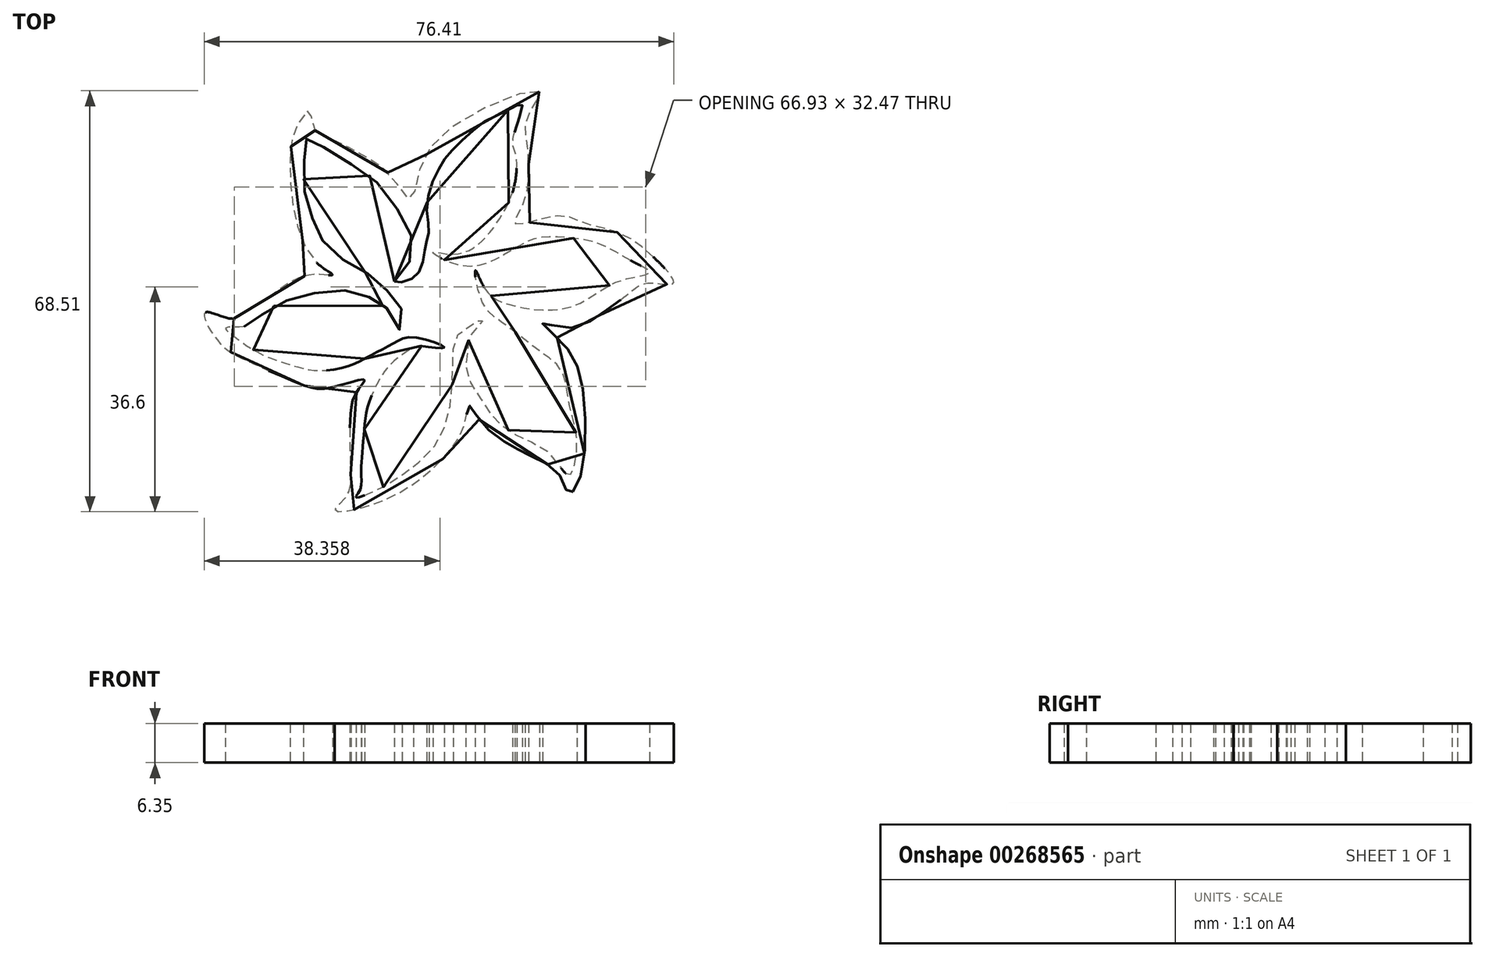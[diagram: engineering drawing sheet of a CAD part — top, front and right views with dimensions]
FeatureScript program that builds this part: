
annotation { "Feature Type Name" : "Feature", "Feature Type Description" : "" }
export const myFeature = defineFeature(function(context is Context, id is Id, definition is map)
    precondition{}
    {
        {
            var Q0;
            Q0=qCreatedBy(makeId("Top.planeOp"),FACE);
            var sketch = newSketch(context, id + "F0", { "sketchPlane" : qUnion([Q0])});
            skPoint(sketch, "E0.34.internal.snap0", {"position": v(38.1, 68.07) * mm});
            skFitSpline(sketch, "E0", {"points": [v(54.35, 68.07) * mm, v(40.9, 62.9) * mm, v(34.76, 54.83) * mm, v(33.41, 50.6) * mm, v(30.53, 54.06) * mm, v(26.11, 57.52) * mm, v(20.54, 60.4) * mm, v(17.47, 62.51) * mm, v(17.09, 65.2) * mm, v(15.36, 63.28) * mm, v(14.01, 59.44) * mm, v(14.01, 51.95) * mm, v(15.36, 45.23) * mm, v(18.43, 40.04) * mm, v(20.74, 38.32) * mm, v(17.09, 38.32) * mm, v(11.13, 35.24) * mm, v(6.52, 32.17) * mm, v(4.03, 31.2) * mm, v(0, 32.17) * mm, v(2.1, 27.56) * mm, v(6.14, 24.68) * mm, v(11.13, 22.37) * mm, v(15.74, 20.45) * mm, v(19.97, 19.88) * mm, v(25.92, 21.22) * mm, v(24.58, 19.1) * mm, v(23.62, 14.3) * mm, v(23.62, 8.35) * mm, v(23.62, 3.94) * mm, v(22.47, 1.63) * mm, v(21.12, 0) * mm, v(23.76, 0) * mm, v(31.1, 2.6) * mm, v(38.1, 7.77) * mm, v(42.19, 13.88) * mm, v(43.02, 17) * mm, v(44.75, 14.54) * mm, v(49.54, 10.66) * mm, v(53, 8.86) * mm, v(57.66, 5.75) * mm, v(59.15, 2.79) * mm, v(60.88, 4.9) * mm, v(61.45, 19.69) * mm, v(58.19, 27.18) * mm, v(54.92, 30.44) * mm, v(58.96, 29.67) * mm, v(65.3, 32.55) * mm, v(69.13, 35.43) * mm, v(72.02, 36.97) * mm, v(76.2, 36.97) * mm, v(73.36, 40.81) * mm, v(67.6, 45.04) * mm, v(61.64, 46.77) * mm, v(57.23, 47.92) * mm, v(50.5, 46.57) * mm, v(51.85, 50.03) * mm, v(52.62, 55.4) * mm, v(52.43, 59.63) * mm, v(52.43, 63.86) * mm, v(54.35, 68.07) * mm]});
            skFitSpline(sketch, "E1", {"points": [v(30.83, 37.2) * mm, v(33.13, 40.17) * mm, v(33.63, 44.46) * mm, v(31, 49.4) * mm, v(26.7, 54.5) * mm, v(21.44, 57.63) * mm, v(17.32, 60.4) * mm, v(16.5, 60.4) * mm, v(16.17, 57.8) * mm, v(16.17, 51.95) * mm, v(17.48, 47.42) * mm, v(18.97, 44.13) * mm, v(22.42, 40.83) * mm, v(26.7, 38.36) * mm, v(29.67, 35.73) * mm, v(31.81, 33.25) * mm, v(31.81, 29.3) * mm, v(30.33, 32.1) * mm, v(27.7, 33.91) * mm, v(25.72, 35.23) * mm, v(20.54, 35.73) * mm, v(15.34, 34.74) * mm, v(10.73, 32.93) * mm, v(7.43, 30.29) * mm, v(5.46, 29.8) * mm, v(3.32, 29.63) * mm, v(4.47, 28.48) * mm, v(6.45, 27) * mm, v(10.4, 24.85) * mm, v(15.5, 23.2) * mm, v(18.47, 22.71) * mm, v(23.58, 23.54) * mm, v(27.2, 25.35) * mm, v(30.66, 27.16) * mm, v(33.96, 28.15) * mm, v(38.9, 26.5) * mm, v(35.77, 26.67) * mm, v(34.45, 26.67) * mm, v(31.65, 25.02) * mm, v(28.85, 22.05) * mm, v(26.54, 17.11) * mm, v(25.88, 13) * mm, v(25.55, 8.88) * mm, v(25.39, 6.08) * mm, v(25.22, 3.28) * mm, v(24.57, 2.12) * mm, v(28.35, 3.44) * mm, v(32.97, 6.4) * mm, v(37.41, 10.52) * mm, v(39.72, 16.12) * mm, v(40.21, 21.07) * mm, v(40.38, 25.84) * mm, v(41.2, 28.64) * mm, v(45.49, 31.28) * mm, v(43.34, 28.8) * mm, v(42.69, 25.84) * mm, v(42.52, 22.55) * mm, v(44.33, 18.92) * mm, v(46.64, 15.46) * mm, v(49.1, 13.16) * mm, v(52.57, 11.35) * mm, v(56.47, 8.86) * mm, v(59.28, 5.71) * mm, v(60.48, 11.51) * mm, v(59.32, 16.95) * mm, v(58, 22.71) * mm, v(54.71, 25.68) * mm, v(50.92, 28.64) * mm, v(47.8, 30.95) * mm, v(45, 34.08) * mm, v(44, 39.02) * mm, v(45.16, 36.71) * mm, v(46.97, 34.57) * mm, v(49.1, 33.58) * mm, v(54.55, 32.6) * mm, v(60.8, 33.58) * mm, v(67.56, 37.37) * mm, v(72.34, 38.7) * mm, v(69.2, 40.67) * mm, v(64.26, 43.3) * mm, v(58, 44.46) * mm, v(53, 43.96) * mm, v(47.63, 41) * mm, v(41.37, 39.84) * mm, v(37.08, 41.99) * mm, v(40.05, 41.66) * mm, v(44.5, 43.3) * mm, v(47.8, 47.26) * mm, v(50.1, 51.95) * mm, v(50.6, 57.8) * mm, v(50.1, 60.4) * mm, v(51.58, 66.03) * mm, v(49.44, 65.21) * mm, v(45.49, 63.23) * mm, v(40.54, 58.95) * mm, v(38.07, 55.66) * mm, v(36.1, 49.56) * mm, v(36.43, 45.28) * mm, v(35.93, 43.3) * mm, v(35.1, 39.35) * mm, v(32.97, 37.37) * mm, v(30.83, 37.2) * mm]});
            skSolve(sketch);
        }
        {
            var Q0;
            Q0 = qSketchRegion(id + "F0", true);
            extrude(context, id + "F1", {"entities" : qUnion([Q0]), "depth" : 6.35 * mm});
        }
    });
